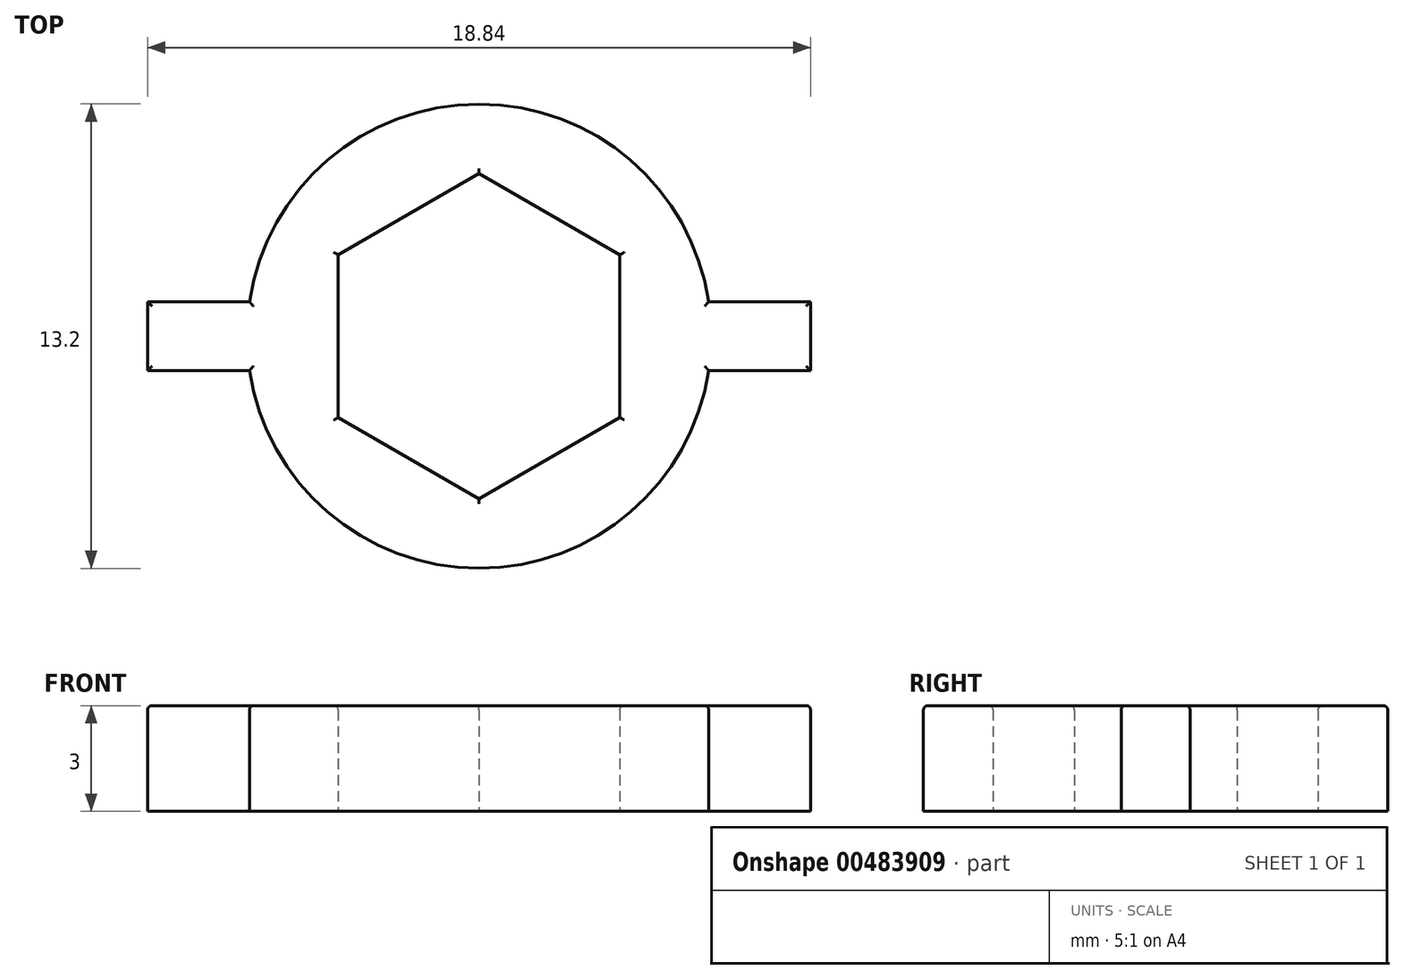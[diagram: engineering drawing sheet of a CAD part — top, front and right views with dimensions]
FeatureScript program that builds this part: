
annotation { "Feature Type Name" : "Feature", "Feature Type Description" : "" }
export const myFeature = defineFeature(function(context is Context, id is Id, definition is map)
    precondition{}
    {
        {
            var Q0;
            Q0=qCreatedBy(makeId("Top.planeOp"),FACE);
            var sketch = newSketch(context, id + "F0", { "sketchPlane" : qUnion([Q0])});
            skLineSegment(sketch, "E0.0", {"start": v(4, 2.3) * mm, "end": v(4, -2.3) * mm});
            skLineSegment(sketch, "E0.1", {"start": v(4, -2.3) * mm, "end": v(0, -4.62) * mm});
            skLineSegment(sketch, "E0.2", {"start": v(0, -4.62) * mm, "end": v(-4, -2.3) * mm});
            skLineSegment(sketch, "E0.3", {"start": v(-4, -2.3) * mm, "end": v(-4, 2.3) * mm});
            skLineSegment(sketch, "E0.4", {"start": v(-4, 2.3) * mm, "end": v(0, 4.62) * mm});
            skLineSegment(sketch, "E0.5", {"start": v(0, 4.62) * mm, "end": v(4, 2.3) * mm});
            skArc(sketch, "E1", {"start": v(6.52, 0.98) * mm, "mid": v(0, 6.6) * mm, "end": v(-6.52, 0.98) * mm});
            skLineSegment(sketch, "E2.bottom", {"start": v(9.42, -0.98) * mm, "end": v(6.52, -0.98) * mm});
            skLineSegment(sketch, "E2.top", {"start": v(9.42, 0.98) * mm, "end": v(6.52, 0.98) * mm});
            skLineSegment(sketch, "E2.left", {"start": v(9.42, -0.98) * mm, "end": v(9.42, 0.98) * mm});
            skLineSegment(sketch, "E2.right", {"start": v(-9.42, -0.98) * mm, "end": v(-9.42, 0.98) * mm});
            skLineSegment(sketch, "E3.trimOffspring", {"start": v(-6.52, 0.98) * mm, "end": v(-9.42, 0.98) * mm});
            skLineSegment(sketch, "E4.trimOffspring", {"start": v(-6.52, -0.98) * mm, "end": v(-9.42, -0.98) * mm});
            skArc(sketch, "E5.trimOffspring", {"start": v(-6.52, -0.98) * mm, "mid": v(0, -6.6) * mm, "end": v(6.52, -0.98) * mm});
            skSolve(sketch);
        }
        {
            var Q0;
            Q0 = qSketchRegion(id + "F0", true);
            extrude(context, id + "F1", {"entities" : qUnion([Q0]), "depth" : 3 * mm});
        }
        {
            var Q0;
            Q0=makeQuery(id+"F1.opExtrude","CAP_FACE",FACE,{"disambiguationData":[OSD([sQuery(id+"F0.wireOp",EDGE,"E0.0"),sQuery(id+"F0.wireOp",EDGE,"E0.1"),sQuery(id+"F0.wireOp",EDGE,"E0.2"),sQuery(id+"F0.wireOp",EDGE,"E0.3"),sQuery(id+"F0.wireOp",EDGE,"E0.4"),sQuery(id+"F0.wireOp",EDGE,"E0.5"),sQuery(id+"F0.wireOp",EDGE,"E1"),sQuery(id+"F0.wireOp",EDGE,"E2.bottom"),sQuery(id+"F0.wireOp",EDGE,"E2.top"),sQuery(id+"F0.wireOp",EDGE,"E2.left"),sQuery(id+"F0.wireOp",EDGE,"E2.right"),sQuery(id+"F0.wireOp",EDGE,"E3.trimOffspring"),sQuery(id+"F0.wireOp",EDGE,"E4.trimOffspring"),sQuery(id+"F0.wireOp",EDGE,"E5.trimOffspring")])],"isStart":false});
            fillet(context, id + "F2", {"entities" : qUnion([Q0]), "tangentPropagation" : true, "radius" : 0.13 * mm, "defaultsChanged" : true, "vertexSettings" : [], "allowEdgeOverflow" : false});
        }
    });
